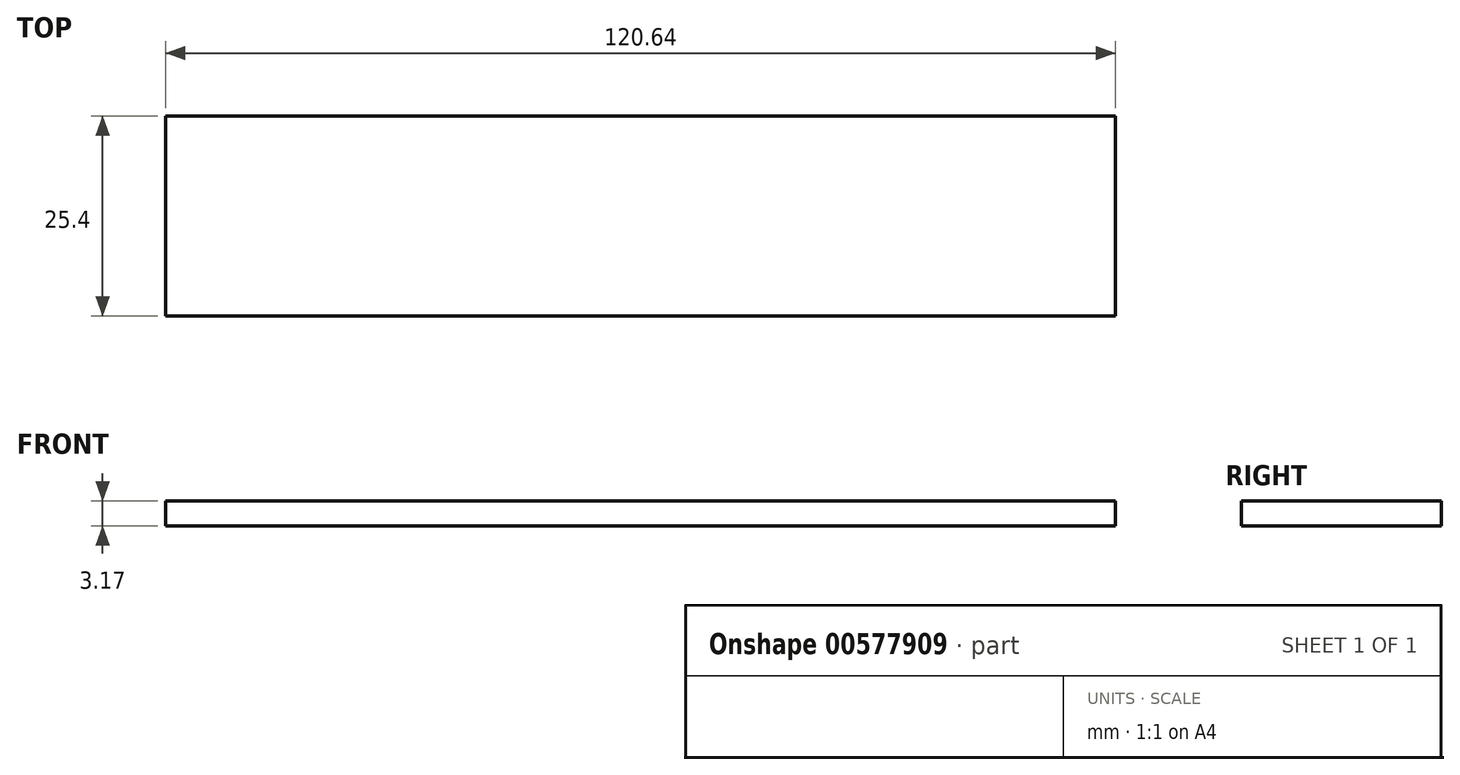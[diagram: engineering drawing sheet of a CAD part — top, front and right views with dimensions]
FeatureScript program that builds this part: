
annotation { "Feature Type Name" : "Feature", "Feature Type Description" : "" }
export const myFeature = defineFeature(function(context is Context, id is Id, definition is map)
    precondition{}
    {
        {
            var Q0;
            Q0=qCreatedBy(makeId("Top.planeOp"),FACE);
            var sketch = newSketch(context, id + "F0", { "sketchPlane" : qUnion([Q0])});
            skLineSegment(sketch, "E0.bottom", {"start": v(60.33, -12.7) * mm, "end": v(-60.33, -12.7) * mm});
            skLineSegment(sketch, "E0.top", {"start": v(60.33, 12.7) * mm, "end": v(-60.33, 12.7) * mm});
            skLineSegment(sketch, "E0.left", {"start": v(60.33, -12.7) * mm, "end": v(60.33, 12.7) * mm});
            skLineSegment(sketch, "E0.right", {"start": v(-60.33, -12.7) * mm, "end": v(-60.33, 12.7) * mm});
            skPoint(sketch, "E0.middle", {"position": v(0, 0) * mm});
            skSolve(sketch);
        }
        {
            var Q0;
            Q0 = qSketchRegion(id + "F0", true);
            extrude(context, id + "F1", {"entities" : qUnion([Q0]), "depth" : 3.17 * mm, "offsetDistance" : 25.4 * mm});
        }
    });
